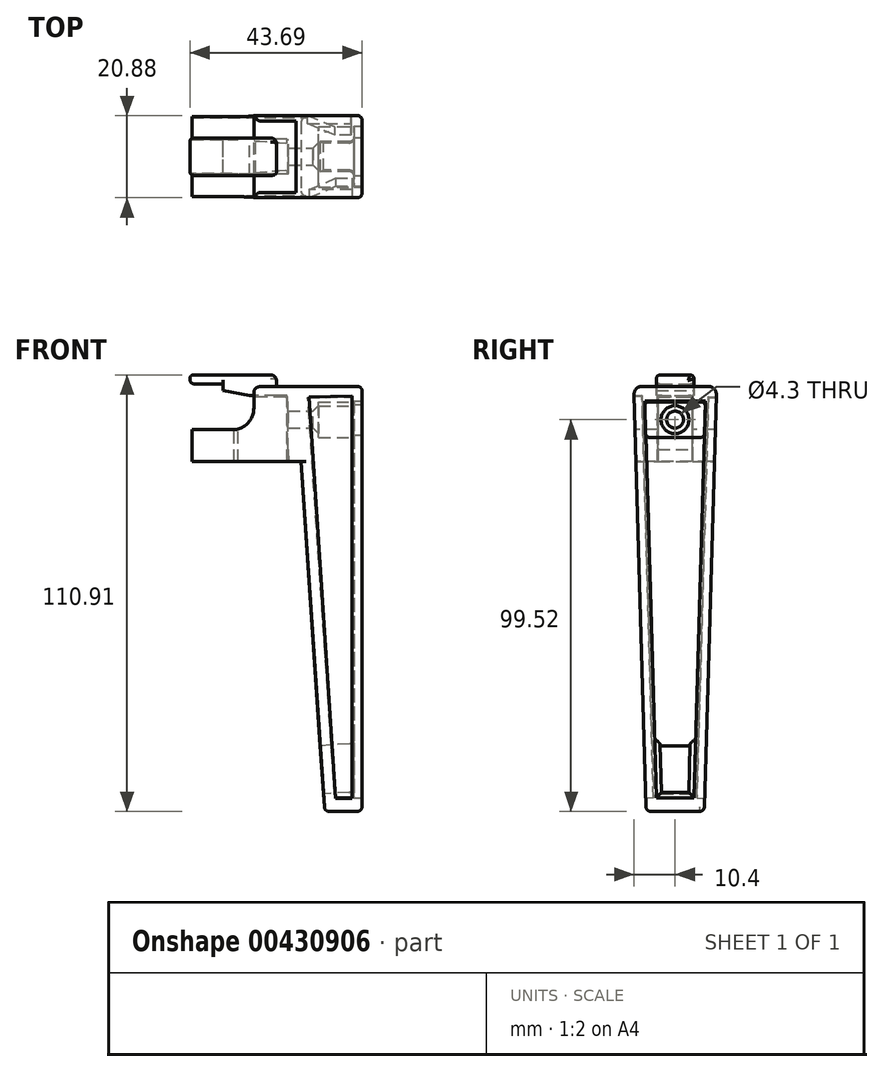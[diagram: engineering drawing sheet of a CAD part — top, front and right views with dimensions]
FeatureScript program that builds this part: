
annotation { "Feature Type Name" : "Feature", "Feature Type Description" : "" }
export const myFeature = defineFeature(function(context is Context, id is Id, definition is map)
    precondition{}
    {
        {
            var Q0;
            Q0=qCreatedBy(makeId("Front.planeOp"),FACE);
            var sketch = newSketch(context, id + "F0", { "sketchPlane" : qUnion([Q0])});
            skLineSegment(sketch, "E0.bottom", {"start": v(-55.85, 16) * mm, "end": v(-25.85, 16) * mm});
            skLineSegment(sketch, "E0.top", {"start": v(-55.85, -3) * mm, "end": v(-25.85, -3) * mm});
            skLineSegment(sketch, "E0.left", {"start": v(-55.85, 16) * mm, "end": v(-55.85, -3) * mm});
            skLineSegment(sketch, "E0.right", {"start": v(-25.85, 16) * mm, "end": v(-25.85, -3) * mm});
            skSolve(sketch);
        }
        {
            var Q0;
            Q0=qSketchRegion(id+"F0",true);
            extrude(context, id + "F1", {"entities" : qUnion([Q0]), "endBound" : BoundingType.SYMMETRIC, "depth" : 21 * mm});
        }
        {
            var Q0;
            Q0=qCreatedBy(makeId("Front.planeOp"),FACE);
            var sketch = newSketch(context, id + "F2", { "sketchPlane" : qUnion([Q0])});
            skLineSegment(sketch, "E1", {"start": v(-31.43, 0) * mm, "end": v(-31.43, 13.4) * mm});
            skPoint(sketch, "E2.endSnap0", {"position": v(-44.03, 0) * mm});
            skLineSegment(sketch, "E3", {"start": v(-48.29, 16.5) * mm, "end": v(-56.03, 16.5) * mm});
            skLineSegment(sketch, "E4", {"start": v(-56.03, 16.5) * mm, "end": v(-56.03, 0) * mm});
            skLineSegment(sketch, "E5", {"start": v(-48.27, 14.9) * mm, "end": v(-39.71, 13.53) * mm});
            skLineSegment(sketch, "E6", {"start": v(-56.03, 0) * mm, "end": v(-56.03, -4.06) * mm});
            skLineSegment(sketch, "E7", {"start": v(-56.03, -4.06) * mm, "end": v(-31.33, -4.06) * mm});
            skLineSegment(sketch, "E8", {"start": v(-31.43, 0) * mm, "end": v(-31.33, -4.06) * mm});
            skLineSegment(sketch, "E9", {"start": v(-39.71, 13.53) * mm, "end": v(-31.43, 13.4) * mm});
            skLineSegment(sketch, "E10", {"start": v(-48.29, 16.5) * mm, "end": v(-48.27, 14.9) * mm});
            skSolve(sketch);
        }
        {
            var Q0;
            Q0=qSketchRegion(id+"F2",true);
            extrude(context, id + "F3", {"entities" : qUnion([Q0]), "operationType" : NewBodyOperationType.REMOVE, "endBound" : BoundingType.SYMMETRIC, "depth" : 8.7 * mm});
        }
        {
            var Q0;
            Q0=qCreatedBy(makeId("Front.planeOp"),FACE);
            var sketch = newSketch(context, id + "F4", { "sketchPlane" : qUnion([Q0])});
            skLineSegment(sketch, "E11.bottom", {"start": v(-56.13, 16.06) * mm, "end": v(-45.63, 16.06) * mm});
            skLineSegment(sketch, "E11.top", {"start": v(-56.13, 5.06) * mm, "end": v(-45.63, 5.06) * mm});
            skLineSegment(sketch, "E11.left", {"start": v(-56.13, 16.06) * mm, "end": v(-56.13, 5.06) * mm});
            skPoint(sketch, "E12", {"position": v(-56.48, 10.64) * mm});
            skArc(sketch, "E13", {"start": v(-45.63, 5.06) * mm, "mid": v(-40.13, 10.56) * mm, "end": v(-45.63, 16.06) * mm});
            skLineSegment(sketch, "E14", {"start": v(-45.63, 16.06) * mm, "end": v(-40.13, 16.06) * mm});
            skPoint(sketch, "E14.endSnap0", {"position": v(-40.13, 10.56) * mm});
            skLineSegment(sketch, "E15", {"start": v(-40.13, 16.06) * mm, "end": v(-40.13, 10.56) * mm});
            skSolve(sketch);
        }
        {
            var Q0;
            Q0=qCreatedBy(makeId("Top.planeOp"),FACE);
            var sketch = newSketch(context, id + "F5", { "sketchPlane" : qUnion([Q0])});
            skLineSegment(sketch, "E16", {"start": v(-45.21, -4.43) * mm, "end": v(-31.66, -3.38) * mm});
            skLineSegment(sketch, "E17", {"start": v(-31.66, -3.38) * mm, "end": v(-31.66, -4.46) * mm});
            skLineSegment(sketch, "E18", {"start": v(-31.66, -4.46) * mm, "end": v(-45.21, -4.43) * mm});
            skLineSegment(sketch, "E19.MirrorCS", {"start": v(-45.21, 4.43) * mm, "end": v(-31.66, 3.38) * mm});
            skLineSegment(sketch, "E20.MirrorCS", {"start": v(-31.66, 4.46) * mm, "end": v(-45.21, 4.43) * mm});
            skLineSegment(sketch, "E21.MirrorCS", {"start": v(-31.66, 3.38) * mm, "end": v(-31.66, 4.46) * mm});
            skSolve(sketch);
        }
        {
            var Q0;
            Q0=qSketchRegion(id+"F5",true);
            extrude(context, id + "F6", {"entities" : qUnion([Q0]), "operationType" : NewBodyOperationType.REMOVE, "endBound" : BoundingType.SYMMETRIC, "oppositeDirection" : true, "depth" : 27.5 * mm, "hasSecondDirection" : true, "secondDirectionOppositeDirection" : true, "secondDirectionDepth" : 25 * mm});
        }
        {
            var Q0;
            Q0=qSketchRegion(id+"F4",true);
            var Q1;
            Q1=qConstructionFilter(qBodyType(qCreatedBy(id+"F4",EDGE),BodyType.WIRE),ConstructionObject.NO);
            extrude(context, id + "F7", {"entities" : qUnion([Q0]), "operationType" : NewBodyOperationType.REMOVE, "surfaceEntities" : qUnion([Q1]), "endBound" : BoundingType.SYMMETRIC, "depth" : 21 * mm});
        }
        {
            var Q0;
            Q0=qCreatedBy(makeId("Front.planeOp"),FACE);
            var sketch = newSketch(context, id + "F8", { "sketchPlane" : qUnion([Q0])});
            skLineSegment(sketch, "E22", {"start": v(-56.34, 19.01) * mm, "end": v(-34.37, 19.01) * mm});
            skLineSegment(sketch, "E23", {"start": v(-34.37, 19.01) * mm, "end": v(-34.37, 13.72) * mm});
            skLineSegment(sketch, "E24", {"start": v(-34.37, 13.72) * mm, "end": v(-41.19, 13.72) * mm});
            skLineSegment(sketch, "E25", {"start": v(-41.19, 13.72) * mm, "end": v(-47.93, 15.07) * mm});
            skLineSegment(sketch, "E26", {"start": v(-47.93, 15.07) * mm, "end": v(-47.93, 16.73) * mm});
            skLineSegment(sketch, "E27", {"start": v(-47.93, 16.73) * mm, "end": v(-56.34, 16.73) * mm});
            skLineSegment(sketch, "E28", {"start": v(-56.34, 16.73) * mm, "end": v(-56.34, 19.01) * mm});
            skSolve(sketch);
        }
        {
            var Q0;
            Q0=qSketchRegion(id+"F8",true);
            extrude(context, id + "F9", {"entities" : qUnion([Q0]), "operationType" : NewBodyOperationType.ADD, "endBound" : BoundingType.SYMMETRIC, "depth" : 9.5 * mm});
        }
        {
            var Q0;
            Q0=makeQuery(id+"F9.opExtrude","CAP_EDGE",EDGE,{"disambiguationData":[OSD([sQuery(id+"F8.wireOp",EDGE,"E22")])],"isStart":false});
            var Q1;
            Q1=makeQuery(id+"F9.opExtrude","CAP_EDGE",EDGE,{"disambiguationData":[OSD([sQuery(id+"F8.wireOp",EDGE,"E23")])],"isStart":false});
            var Q2;
            Q2=makeQuery(id+"F9.opExtrude","CAP_EDGE",EDGE,{"disambiguationData":[OSD([sQuery(id+"F8.wireOp",EDGE,"E22")])],"isStart":true});
            var Q3;
            Q3=makeQuery(id+"F9.opExtrude","SWEPT_EDGE",EDGE,{"disambiguationData":[OSD([sQuery(id+"F8.wireOp",EDGE,"E27"),sQuery(id+"F8.wireOp",EDGE,"E28")])]});
            fillet(context, id + "F10", {"entities" : qUnion([Q0, Q1, Q2, Q3]), "radius" : 1 * mm, "tangentPropagation" : true, "allowEdgeOverflow" : false});
        }
        {
            var Q0;
            Q0=makeQuery(id+"F1.opExtrude","CAP_EDGE",EDGE,{"disambiguationData":[OSD([sQuery(id+"F0.wireOp",EDGE,"E0.bottom")])],"isStart":true});
            var Q1;
            Q1=makeQuery(id+"F7.boolean.opBoolean","COPY",EDGE,{"derivedFrom":makeQuery(id+"F7.opExtrude","CAP_EDGE",EDGE,{"disambiguationData":[OSD([sQuery(id+"F4.wireOp",EDGE,"E15")])],"isStart":true})});
            var Q2;
            Q2=makeQuery(id+"F7.boolean.opBoolean","COPY",EDGE,{"derivedFrom":makeQuery(id+"F7.opExtrude","CAP_EDGE",EDGE,{"disambiguationData":[OSD([sQuery(id+"F4.wireOp",EDGE,"E15")])],"isStart":false})});
            var Q3;
            Q3=makeQuery(id+"F1.opExtrude","CAP_EDGE",EDGE,{"disambiguationData":[OSD([sQuery(id+"F0.wireOp",EDGE,"E0.bottom")])],"isStart":false});
            var Q4;
            {var subQ0=sQuery(id+"F0.wireOp",EDGE,"E0.bottom");var subQ1=makeQuery(id+"F1.opExtrude","SWEPT_FACE",FACE,{"disambiguationData":[OSD([subQ0])]});var subQ2=makeQuery(id+"F7.opExtrude","SWEPT_FACE",FACE,{"disambiguationData":[OSD([sQuery(id+"F4.wireOp",EDGE,"E15")])]});Q4=makeQuery(id+"F9.boolean.opBoolean","SPLIT",EDGE,{"disambiguationData":[TD([makeQuery(id+"F1.opExtrude","CAP_FACE",FACE,{"disambiguationData":[OSD([subQ0,sQuery(id+"F0.wireOp",EDGE,"E0.top"),sQuery(id+"F0.wireOp",EDGE,"E0.left"),sQuery(id+"F0.wireOp",EDGE,"E0.right")])],"isStart":false})])],"derivedFrom":makeQuery(id+"F7.boolean.opBoolean","INTERSECT",EDGE,{"derivedFrom":[subQ1,subQ2]})});}
            var Q5;
            Q5=makeQuery(id+"F9.opExtrude","SWEPT_EDGE",EDGE,{"disambiguationData":[OSD([sQuery(id+"F8.wireOp",EDGE,"E22"),sQuery(id+"F8.wireOp",EDGE,"E23")])]});
            var Q6;
            {var subQ0=sQuery(id+"F0.wireOp",EDGE,"E0.bottom");var subQ1=makeQuery(id+"F1.opExtrude","SWEPT_FACE",FACE,{"disambiguationData":[OSD([subQ0])]});var subQ2=makeQuery(id+"F7.opExtrude","SWEPT_FACE",FACE,{"disambiguationData":[OSD([sQuery(id+"F4.wireOp",EDGE,"E15")])]});Q6=makeQuery(id+"F9.boolean.opBoolean","SPLIT",EDGE,{"disambiguationData":[TD([makeQuery(id+"F1.opExtrude","CAP_FACE",FACE,{"disambiguationData":[OSD([subQ0,sQuery(id+"F0.wireOp",EDGE,"E0.top"),sQuery(id+"F0.wireOp",EDGE,"E0.left"),sQuery(id+"F0.wireOp",EDGE,"E0.right")])],"isStart":true})])],"derivedFrom":makeQuery(id+"F7.boolean.opBoolean","INTERSECT",EDGE,{"derivedFrom":[subQ1,subQ2]})});}
            var Q7;
            {var subQ0=sQuery(id+"F8.wireOp",EDGE,"E22");Q7=makeQuery(id+"F10.opFillet","BLEND_EDGE",EDGE,{"blendedFrom":[makeQuery(id+"F9.opExtrude","SWEPT_EDGE",EDGE,{"disambiguationData":[OSD([subQ0,sQuery(id+"F8.wireOp",EDGE,"E28")])]}),makeQuery(id+"F9.opExtrude","SWEPT_FACE",FACE,{"disambiguationData":[OSD([subQ0])]})],"blendedInto":[makeQuery(id+"F9.opExtrude","SWEPT_FACE",FACE,{"disambiguationData":[OSD([subQ0])]})]});}
            var Q8;
            {var subQ0=sQuery(id+"F8.wireOp",EDGE,"E28");Q8=makeQuery(id+"F10.opFillet","BLEND_EDGE",EDGE,{"blendedFrom":[makeQuery(id+"F9.opExtrude","SWEPT_EDGE",EDGE,{"disambiguationData":[OSD([sQuery(id+"F8.wireOp",EDGE,"E22"),subQ0])]}),makeQuery(id+"F9.opExtrude","SWEPT_FACE",FACE,{"disambiguationData":[OSD([subQ0])]})],"blendedInto":[makeQuery(id+"F9.opExtrude","SWEPT_FACE",FACE,{"disambiguationData":[OSD([subQ0])]})]});}
            fillet(context, id + "F11", {"entities" : qUnion([Q0, Q1, Q2, Q3, Q4, Q5, Q6, Q7, Q8]), "radius" : 1.5 * mm, "tangentPropagation" : true, "allowEdgeOverflow" : false});
        }
        {
            var Q0;
            Q0=qCreatedBy(makeId("Front.planeOp"),FACE);
            var sketch = newSketch(context, id + "F12", { "sketchPlane" : qUnion([Q0])});
            skLineSegment(sketch, "E29", {"start": v(-25.15, 16.1) * mm, "end": v(-12.65, 16.1) * mm});
            skLineSegment(sketch, "E30", {"start": v(-12.65, 16.1) * mm, "end": v(-12.65, -91.9) * mm});
            skLineSegment(sketch, "E31", {"start": v(-12.65, -91.9) * mm, "end": v(-22.15, -91.9) * mm});
            skLineSegment(sketch, "E32", {"start": v(-22.15, -91.9) * mm, "end": v(-29.41, 16.1) * mm});
            skLineSegment(sketch, "E33", {"start": v(-29.41, 16.1) * mm, "end": v(-25.15, 16.1) * mm});
            skLineSegment(sketch, "E34.0", {"start": v(-15.65, -88.9) * mm, "end": v(-19.34, -88.9) * mm});
            skLineSegment(sketch, "E34.1", {"start": v(-15.65, 13.1) * mm, "end": v(-15.65, -88.9) * mm});
            skLineSegment(sketch, "E34.2", {"start": v(-19.34, -88.9) * mm, "end": v(-26.2, 13.1) * mm});
            skLineSegment(sketch, "E34.3", {"start": v(-26.2, 13.1) * mm, "end": v(-25.15, 13.1) * mm});
            skLineSegment(sketch, "E34.4", {"start": v(-25.15, 13.1) * mm, "end": v(-15.65, 13.1) * mm});
            skSolve(sketch);
        }
        {
            var Q0;
            Q0 = qSketchRegion(id + "F12", true);
            var Q1;
            Q1=makeQuery(id+"F12.imprint","IMPRINT",FACE,{"disambiguationData":[TD([[makeQuery(id+"F12.imprint","IMPRINT",EDGE,{"derivedFrom":sQuery(id+"F12.wireOp",EDGE,"E34.0")}),-1.0]])]});
            extrude(context, id + "F13", {"entities" : qUnion([Q0, Q1]), "operationType" : NewBodyOperationType.ADD, "endBound" : BoundingType.SYMMETRIC, "depth" : 21 * mm});
        }
        {
            var Q0;
            Q0=qCreatedBy(makeId("Right.planeOp"),FACE);
            var sketch = newSketch(context, id + "F14", { "sketchPlane" : qUnion([Q0])});
            skLineSegment(sketch, "E35", {"start": v(0, -91.9) * mm, "end": v(0, -91.9) * mm});
            skLineSegment(sketch, "E36", {"start": v(-10.5, 16.1) * mm, "end": v(-7.33, -94.31) * mm});
            skLineSegment(sketch, "E37", {"start": v(-7.33, -94.31) * mm, "end": v(-11, -94.42) * mm});
            skLineSegment(sketch, "E38", {"start": v(-11, -94.42) * mm, "end": v(-10.5, 16.1) * mm});
            skLineSegment(sketch, "E39.MirrorCS", {"start": v(10.5, 16.1) * mm, "end": v(7.33, -94.31) * mm});
            skLineSegment(sketch, "E40.MirrorCS", {"start": v(11, -94.42) * mm, "end": v(10.5, 16.1) * mm});
            skLineSegment(sketch, "E41.MirrorCS", {"start": v(7.33, -94.31) * mm, "end": v(11, -94.42) * mm});
            skSolve(sketch);
        }
        {
            var Q0;
            Q0 = qSketchRegion(id + "F14", true);
            extrude(context, id + "F15", {"entities" : qUnion([Q0]), "operationType" : NewBodyOperationType.REMOVE, "endBound" : BoundingType.THROUGH_ALL, "oppositeDirection" : true, "depth" : 25 * mm});
        }
        {
            var Q0;
            Q0=makeQuery(id+"F13.opExtrude","SWEPT_FACE",FACE,{"disambiguationData":[OSD([sQuery(id+"F12.wireOp",EDGE,"E30")])]});
            var sketch = newSketch(context, id + "F16", { "sketchPlane" : qUnion([Q0])});
            skLineSegment(sketch, "E42", {"start": v(0, 13.26) * mm, "end": v(0.34, 13.26) * mm});
            skLineSegment(sketch, "E43", {"start": v(7.65, 11.09) * mm, "end": v(7.44, 4.09) * mm});
            skLineSegment(sketch, "E44.MirrorCS", {"start": v(-7.72, 11.09) * mm, "end": v(-7.52, 4.09) * mm});
            skLineSegment(sketch, "E45", {"start": v(-6.72, 12.11) * mm, "end": v(6.65, 12.11) * mm});
            skLineSegment(sketch, "E46", {"start": v(-6.52, 3.12) * mm, "end": v(6.45, 3.12) * mm});
            skLineSegment(sketch, "E47", {"start": v(0, 10.76) * mm, "end": v(0, 1.77) * mm});
            skPoint(sketch, "E48", {"position": v(-0.04, 7.62) * mm});
            skPoint(sketch, "E49.visualSharp", {"position": v(-7.75, 12.11) * mm});
            skArc(sketch, "E49.filletArc", {"start": v(-6.72, 12.11) * mm, "mid": v(-7.44, 11.81) * mm, "end": v(-7.72, 11.09) * mm});
            skPoint(sketch, "E50.visualSharp", {"position": v(-7.5, 3.12) * mm});
            skArc(sketch, "E50.filletArc", {"start": v(-7.52, 4.09) * mm, "mid": v(-7.22, 3.4) * mm, "end": v(-6.52, 3.12) * mm});
            skPoint(sketch, "E51.visualSharp", {"position": v(7.42, 3.12) * mm});
            skArc(sketch, "E51.filletArc", {"start": v(6.45, 3.12) * mm, "mid": v(7.14, 3.4) * mm, "end": v(7.44, 4.09) * mm});
            skPoint(sketch, "E52.visualSharp", {"position": v(7.68, 12.11) * mm});
            skArc(sketch, "E52.filletArc", {"start": v(7.65, 11.09) * mm, "mid": v(7.36, 11.81) * mm, "end": v(6.65, 12.11) * mm});
            skSolve(sketch);
        }
        {
            var Q0;
            Q0=makeQuery(id+"F16.imprint","IMPRINT",FACE,{"disambiguationData":[TD([[makeQuery(id+"F16.imprint","IMPRINT",EDGE,{"derivedFrom":sQuery(id+"F16.wireOp",EDGE,"E43")}),-1.0]])]});
            var Q1;
            {var subQ0=sQuery(id+"F16.wireOp",EDGE,"E44.MirrorCS");Q1=makeQuery(id+"F16.imprint","IMPRINT",FACE,{"disambiguationData":[TD([[makeQuery(id+"F16.imprint","IMPRINT",EDGE,{"derivedFrom":subQ0}),1.0]])]});}
            extrude(context, id + "F17", {"entities" : qUnion([Q0, Q1]), "operationType" : NewBodyOperationType.REMOVE, "oppositeDirection" : true, "depth" : 11 * mm});
        }
        {
            var Q0;
            Q0=sQuery(id+"F16.wireOp",VERTEX,"E48");
            var Q1;
            Q1=makeQuery(id+"F1.opExtrude","SWEPT_BODY",BODY,{"disambiguationData":[OSD([sQuery(id+"F0.wireOp",EDGE,"E0.bottom"),sQuery(id+"F0.wireOp",EDGE,"E0.top"),sQuery(id+"F0.wireOp",EDGE,"E0.left"),sQuery(id+"F0.wireOp",EDGE,"E0.right")])]});
            hole(context, id + "F18", {"style" : HoleStyle.C_SINK, "endStyle" : HoleEndStyle.THROUGH, "holeDiameter" : 4.3 * mm, "cSinkDiameter" : 7.1 * mm, "cSinkAngle" : 90 * degree, "isTappedThrough" : true, "tappedDepth" : 12 * mm, "tapClearance" : 3, "locations" : qUnion([Q0]), "scope" : qUnion([Q1])});
        }
        {
            var Q0;
            Q0=makeQuery(id+"F15.boolean.opBoolean","COPY",FACE,{"derivedFrom":makeQuery(id+"F15.opExtrude","SWEPT_FACE",FACE,{"disambiguationData":[OSD([sQuery(id+"F14.wireOp",EDGE,"E39.MirrorCS")])]})});
            var sketch = newSketch(context, id + "F19", { "sketchPlane" : qUnion([Q0])});
            skLineSegment(sketch, "E53", {"start": v(15.39, 13.73) * mm, "end": v(15.39, -88.33) * mm});
            skLineSegment(sketch, "E54", {"start": v(15.39, -88.33) * mm, "end": v(19.53, -88.33) * mm});
            skLineSegment(sketch, "E55", {"start": v(19.53, -88.33) * mm, "end": v(26.44, 13.5) * mm});
            skLineSegment(sketch, "E56", {"start": v(26.44, 13.5) * mm, "end": v(15.39, 13.73) * mm});
            skSolve(sketch);
        }
        {
            var Q0;
            Q0 = qSketchRegion(id + "F19", true);
            extrude(context, id + "F20", {"entities" : qUnion([Q0]), "operationType" : NewBodyOperationType.REMOVE, "oppositeDirection" : true, "depth" : 2 * mm});
        }
        {
            var Q0;
            Q0=makeQuery(id+"F15.boolean.opBoolean","COPY",FACE,{"derivedFrom":makeQuery(id+"F15.opExtrude","SWEPT_FACE",FACE,{"disambiguationData":[OSD([sQuery(id+"F14.wireOp",EDGE,"E36")])]})});
            var sketch = newSketch(context, id + "F21", { "sketchPlane" : qUnion([Q0])});
            skLineSegment(sketch, "E57", {"start": v(-26.07, 13.73) * mm, "end": v(-19.39, -88.33) * mm});
            skLineSegment(sketch, "E58", {"start": v(-19.39, -88.33) * mm, "end": v(-15.24, -88.33) * mm});
            skLineSegment(sketch, "E59", {"start": v(-15.24, -88.33) * mm, "end": v(-15.24, -48.93) * mm});
            skLineSegment(sketch, "E60", {"start": v(-15.24, -48.93) * mm, "end": v(-15.24, 13.96) * mm});
            skLineSegment(sketch, "E61", {"start": v(-15.24, 13.96) * mm, "end": v(-26.07, 13.73) * mm});
            skSolve(sketch);
        }
        {
            var Q0;
            Q0=makeQuery(id+"F21.imprint","IMPRINT",FACE,{"disambiguationData":[TD([[makeQuery(id+"F21.imprint","IMPRINT",EDGE,{"derivedFrom":sQuery(id+"F21.wireOp",EDGE,"E57")}),1.0]])]});
            extrude(context, id + "F22", {"entities" : qUnion([Q0]), "operationType" : NewBodyOperationType.REMOVE, "oppositeDirection" : true, "depth" : 2 * mm});
        }
        {
            var Q0;
            {var subQ3=sQuery(id+"F16.wireOp",EDGE,"E43");Q0=makeQuery(id+"F16.imprint","IMPRINT",FACE,{"disambiguationData":[TD([[makeQuery(id+"F16.imprint","IMPRINT",EDGE,{"derivedFrom":subQ3}),1.0]])]});}
            var sketch = newSketch(context, id + "F23", { "sketchPlane" : qUnion([Q0])});
            skLineSegment(sketch, "E62", {"start": v(-7.7, 12.35) * mm, "end": v(-4.8, -88.48) * mm});
            skLineSegment(sketch, "E63.MirrorCS", {"start": v(7.7, 12.35) * mm, "end": v(4.8, -88.48) * mm});
            skLineSegment(sketch, "E64", {"start": v(-4.8, -88.48) * mm, "end": v(4.8, -88.48) * mm});
            skLineSegment(sketch, "E65", {"start": v(-7.7, 12.35) * mm, "end": v(7.7, 12.35) * mm});
            skSolve(sketch);
        }
        {
            var Q0;
            Q0 = qSketchRegion(id + "F23", true);
            extrude(context, id + "F24", {"entities" : qUnion([Q0]), "operationType" : NewBodyOperationType.REMOVE, "oppositeDirection" : true, "depth" : 2 * mm});
        }
        {
            var Q0;
            Q0=makeQuery(id+"F15.boolean.opBoolean","INTERSECT",EDGE,{"derivedFrom":[makeQuery(id+"F13.opExtrude","SWEPT_FACE",FACE,{"disambiguationData":[OSD([sQuery(id+"F12.wireOp",EDGE,"E31")])]}),makeQuery(id+"F15.opExtrude","SWEPT_FACE",FACE,{"disambiguationData":[OSD([sQuery(id+"F14.wireOp",EDGE,"E36")])]})]});
            var Q1;
            Q1=makeQuery(id+"F15.boolean.opBoolean","INTERSECT",EDGE,{"derivedFrom":[makeQuery(id+"F13.opExtrude","SWEPT_FACE",FACE,{"disambiguationData":[OSD([sQuery(id+"F12.wireOp",EDGE,"E30")])]}),makeQuery(id+"F15.opExtrude","SWEPT_FACE",FACE,{"disambiguationData":[OSD([sQuery(id+"F14.wireOp",EDGE,"E36")])]})]});
            var Q2;
            {var subQ0=sQuery(id+"F0.wireOp",EDGE,"E0.top");var subQ5=sQuery(id+"F12.wireOp",EDGE,"E32");Q2=makeQuery(id+"F15.boolean.opBoolean","INTERSECT",EDGE,{"derivedFrom":[makeQuery(id+"F13.boolean.opBoolean","SPLIT",FACE,{"disambiguationData":[TD([makeQuery(id+"F1.opExtrude","SWEPT_FACE",FACE,{"disambiguationData":[OSD([subQ0])]})])],"derivedFrom":makeQuery(id+"F13.opExtrude","SWEPT_FACE",FACE,{"disambiguationData":[OSD([subQ5])]})}),makeQuery(id+"F15.opExtrude","SWEPT_FACE",FACE,{"disambiguationData":[OSD([sQuery(id+"F14.wireOp",EDGE,"E36")])]})]});}
            var Q3;
            {var subQ0=sQuery(id+"F0.wireOp",EDGE,"E0.top");var subQ5=sQuery(id+"F12.wireOp",EDGE,"E32");Q3=makeQuery(id+"F15.boolean.opBoolean","INTERSECT",EDGE,{"derivedFrom":[makeQuery(id+"F13.boolean.opBoolean","SPLIT",FACE,{"disambiguationData":[TD([makeQuery(id+"F1.opExtrude","SWEPT_FACE",FACE,{"disambiguationData":[OSD([subQ0])]})])],"derivedFrom":makeQuery(id+"F13.opExtrude","SWEPT_FACE",FACE,{"disambiguationData":[OSD([subQ5])]})}),makeQuery(id+"F15.opExtrude","SWEPT_FACE",FACE,{"disambiguationData":[OSD([sQuery(id+"F14.wireOp",EDGE,"E39.MirrorCS")])]})]});}
            var Q4;
            Q4=makeQuery(id+"F15.boolean.opBoolean","INTERSECT",EDGE,{"derivedFrom":[makeQuery(id+"F13.opExtrude","SWEPT_FACE",FACE,{"disambiguationData":[OSD([sQuery(id+"F12.wireOp",EDGE,"E31")])]}),makeQuery(id+"F15.opExtrude","SWEPT_FACE",FACE,{"disambiguationData":[OSD([sQuery(id+"F14.wireOp",EDGE,"E39.MirrorCS")])]})]});
            var Q5;
            Q5=makeQuery(id+"F15.boolean.opBoolean","INTERSECT",EDGE,{"derivedFrom":[makeQuery(id+"F13.opExtrude","SWEPT_FACE",FACE,{"disambiguationData":[OSD([sQuery(id+"F12.wireOp",EDGE,"E30")])]}),makeQuery(id+"F15.opExtrude","SWEPT_FACE",FACE,{"disambiguationData":[OSD([sQuery(id+"F14.wireOp",EDGE,"E39.MirrorCS")])]})]});
            var Q6;
            Q6=makeQuery(id+"F13.opExtrude","SWEPT_EDGE",EDGE,{"disambiguationData":[OSD([sQuery(id+"F12.wireOp",EDGE,"E29"),sQuery(id+"F12.wireOp",EDGE,"E30")])]});
            var Q7;
            Q7=makeQuery(id+"F13.opExtrude","SWEPT_EDGE",EDGE,{"disambiguationData":[OSD([sQuery(id+"F12.wireOp",EDGE,"E30"),sQuery(id+"F12.wireOp",EDGE,"E31")])]});
            var Q8;
            Q8=makeQuery(id+"F13.opExtrude","SWEPT_EDGE",EDGE,{"disambiguationData":[OSD([sQuery(id+"F12.wireOp",EDGE,"E31"),sQuery(id+"F12.wireOp",EDGE,"E32")])]});
            fillet(context, id + "F25", {"entities" : qUnion([Q0, Q1, Q2, Q3, Q4, Q5, Q6, Q7, Q8]), "radius" : 1.2 * mm, "tangentPropagation" : true, "allowEdgeOverflow" : false});
        }
        {
            var Q0;
            Q0=makeQuery(id+"F13.opExtrude","CAP_EDGE",EDGE,{"disambiguationData":[OSD([sQuery(id+"F12.wireOp",EDGE,"E29"),sQuery(id+"F12.wireOp",EDGE,"E33")])],"isStart":false});
            var Q1;
            Q1=makeQuery(id+"F13.opExtrude","CAP_EDGE",EDGE,{"disambiguationData":[OSD([sQuery(id+"F12.wireOp",EDGE,"E29"),sQuery(id+"F12.wireOp",EDGE,"E33")])],"isStart":true});
            fillet(context, id + "F26", {"entities" : qUnion([Q0, Q1]), "radius" : 2 * mm, "tangentPropagation" : true, "allowEdgeOverflow" : false});
        }
        {
            var Q0;
            Q0=makeQuery(id+"F9.opExtrude","SWEPT_EDGE",EDGE,{"disambiguationData":[OSD([sQuery(id+"F8.wireOp",EDGE,"E22"),sQuery(id+"F8.wireOp",EDGE,"E28")])]});
            fillet(context, id + "F27", {"entities" : qUnion([Q0]), "radius" : 1 * mm, "tangentPropagation" : true, "rho" : 0.5, "crossSection" : FilletCrossSection.CONIC, "allowEdgeOverflow" : false});
        }
        {
            var Q0;
            {var subQ0=sQuery(id+"F0.wireOp",EDGE,"E0.top");var subQ5=sQuery(id+"F12.wireOp",EDGE,"E32");Q0=makeQuery(id+"F13.boolean.opBoolean","SPLIT",FACE,{"disambiguationData":[TD([makeQuery(id+"F1.opExtrude","SWEPT_FACE",FACE,{"disambiguationData":[OSD([subQ0])]})])],"derivedFrom":makeQuery(id+"F13.opExtrude","SWEPT_FACE",FACE,{"disambiguationData":[OSD([subQ5])]})});}
            var sketch = newSketch(context, id + "F28", { "sketchPlane" : qUnion([Q0])});
            skLineSegment(sketch, "E66", {"start": v(-3.81, -73.5) * mm, "end": v(-3.46, -85.77) * mm});
            skLineSegment(sketch, "E67.MirrorCS", {"start": v(3.81, -73.5) * mm, "end": v(3.46, -85.77) * mm});
            skLineSegment(sketch, "E68", {"start": v(-3.81, -73.5) * mm, "end": v(3.81, -73.5) * mm});
            skLineSegment(sketch, "E69", {"start": v(3.46, -85.77) * mm, "end": v(-3.46, -85.77) * mm});
            skSolve(sketch);
        }
        {
            var Q0;
            Q0 = qSketchRegion(id + "F28", true);
            extrude(context, id + "F29", {"entities" : qUnion([Q0]), "operationType" : NewBodyOperationType.REMOVE, "endBound" : BoundingType.THROUGH_ALL, "oppositeDirection" : true, "depth" : 25 * mm});
        }
        {
            var Q0;
            Q0=makeQuery(id+"F29.boolean.opBoolean","COPY",EDGE,{"derivedFrom":makeQuery(id+"F29.opExtrude","CAP_EDGE",EDGE,{"disambiguationData":[OSD([sQuery(id+"F28.wireOp",EDGE,"E67.MirrorCS")])],"isStart":true})});
            var Q1;
            Q1=makeQuery(id+"F29.boolean.opBoolean","COPY",EDGE,{"derivedFrom":makeQuery(id+"F29.opExtrude","CAP_EDGE",EDGE,{"disambiguationData":[OSD([sQuery(id+"F28.wireOp",EDGE,"E66")])],"isStart":true})});
            var Q2;
            Q2=makeQuery(id+"F29.boolean.opBoolean","COPY",EDGE,{"derivedFrom":makeQuery(id+"F29.opExtrude","CAP_EDGE",EDGE,{"disambiguationData":[OSD([sQuery(id+"F28.wireOp",EDGE,"E69")])],"isStart":true})});
            var Q3;
            Q3=makeQuery(id+"F29.boolean.opBoolean","INTERSECT",EDGE,{"derivedFrom":[makeQuery(id+"F24.boolean.opBoolean","COPY",FACE,{"derivedFrom":makeQuery(id+"F24.opExtrude","CAP_FACE",FACE,{"disambiguationData":[OSD([sQuery(id+"F23.wireOp",EDGE,"E62"),sQuery(id+"F23.wireOp",EDGE,"E63.MirrorCS"),sQuery(id+"F23.wireOp",EDGE,"E64"),sQuery(id+"F23.wireOp",EDGE,"E65")])],"isStart":false})}),makeQuery(id+"F29.opExtrude","SWEPT_FACE",FACE,{"disambiguationData":[OSD([sQuery(id+"F28.wireOp",EDGE,"E66")])]})]});
            var Q4;
            Q4=makeQuery(id+"F29.boolean.opBoolean","INTERSECT",EDGE,{"derivedFrom":[makeQuery(id+"F24.boolean.opBoolean","COPY",FACE,{"derivedFrom":makeQuery(id+"F24.opExtrude","CAP_FACE",FACE,{"disambiguationData":[OSD([sQuery(id+"F23.wireOp",EDGE,"E62"),sQuery(id+"F23.wireOp",EDGE,"E63.MirrorCS"),sQuery(id+"F23.wireOp",EDGE,"E64"),sQuery(id+"F23.wireOp",EDGE,"E65")])],"isStart":false})}),makeQuery(id+"F29.opExtrude","SWEPT_FACE",FACE,{"disambiguationData":[OSD([sQuery(id+"F28.wireOp",EDGE,"E67.MirrorCS")])]})]});
            var Q5;
            Q5=makeQuery(id+"F29.boolean.opBoolean","COPY",EDGE,{"derivedFrom":makeQuery(id+"F29.opExtrude","CAP_EDGE",EDGE,{"disambiguationData":[OSD([sQuery(id+"F28.wireOp",EDGE,"E68")])],"isStart":true})});
            var Q6;
            Q6=makeQuery(id+"F29.boolean.opBoolean","INTERSECT",EDGE,{"derivedFrom":[makeQuery(id+"F24.boolean.opBoolean","COPY",FACE,{"derivedFrom":makeQuery(id+"F24.opExtrude","CAP_FACE",FACE,{"disambiguationData":[OSD([sQuery(id+"F23.wireOp",EDGE,"E62"),sQuery(id+"F23.wireOp",EDGE,"E63.MirrorCS"),sQuery(id+"F23.wireOp",EDGE,"E64"),sQuery(id+"F23.wireOp",EDGE,"E65")])],"isStart":false})}),makeQuery(id+"F29.opExtrude","SWEPT_FACE",FACE,{"disambiguationData":[OSD([sQuery(id+"F28.wireOp",EDGE,"E68")])]})]});
            var Q7;
            Q7=makeQuery(id+"F29.boolean.opBoolean","INTERSECT",EDGE,{"derivedFrom":[makeQuery(id+"F24.boolean.opBoolean","COPY",FACE,{"derivedFrom":makeQuery(id+"F24.opExtrude","CAP_FACE",FACE,{"disambiguationData":[OSD([sQuery(id+"F23.wireOp",EDGE,"E62"),sQuery(id+"F23.wireOp",EDGE,"E63.MirrorCS"),sQuery(id+"F23.wireOp",EDGE,"E64"),sQuery(id+"F23.wireOp",EDGE,"E65")])],"isStart":false})}),makeQuery(id+"F29.opExtrude","SWEPT_FACE",FACE,{"disambiguationData":[OSD([sQuery(id+"F28.wireOp",EDGE,"E69")])]})]});
            fillet(context, id + "F30", {"entities" : qUnion([Q0, Q1, Q2, Q3, Q4, Q5, Q6, Q7]), "radius" : 1.2 * mm, "tangentPropagation" : true, "allowEdgeOverflow" : false});
        }
    });
